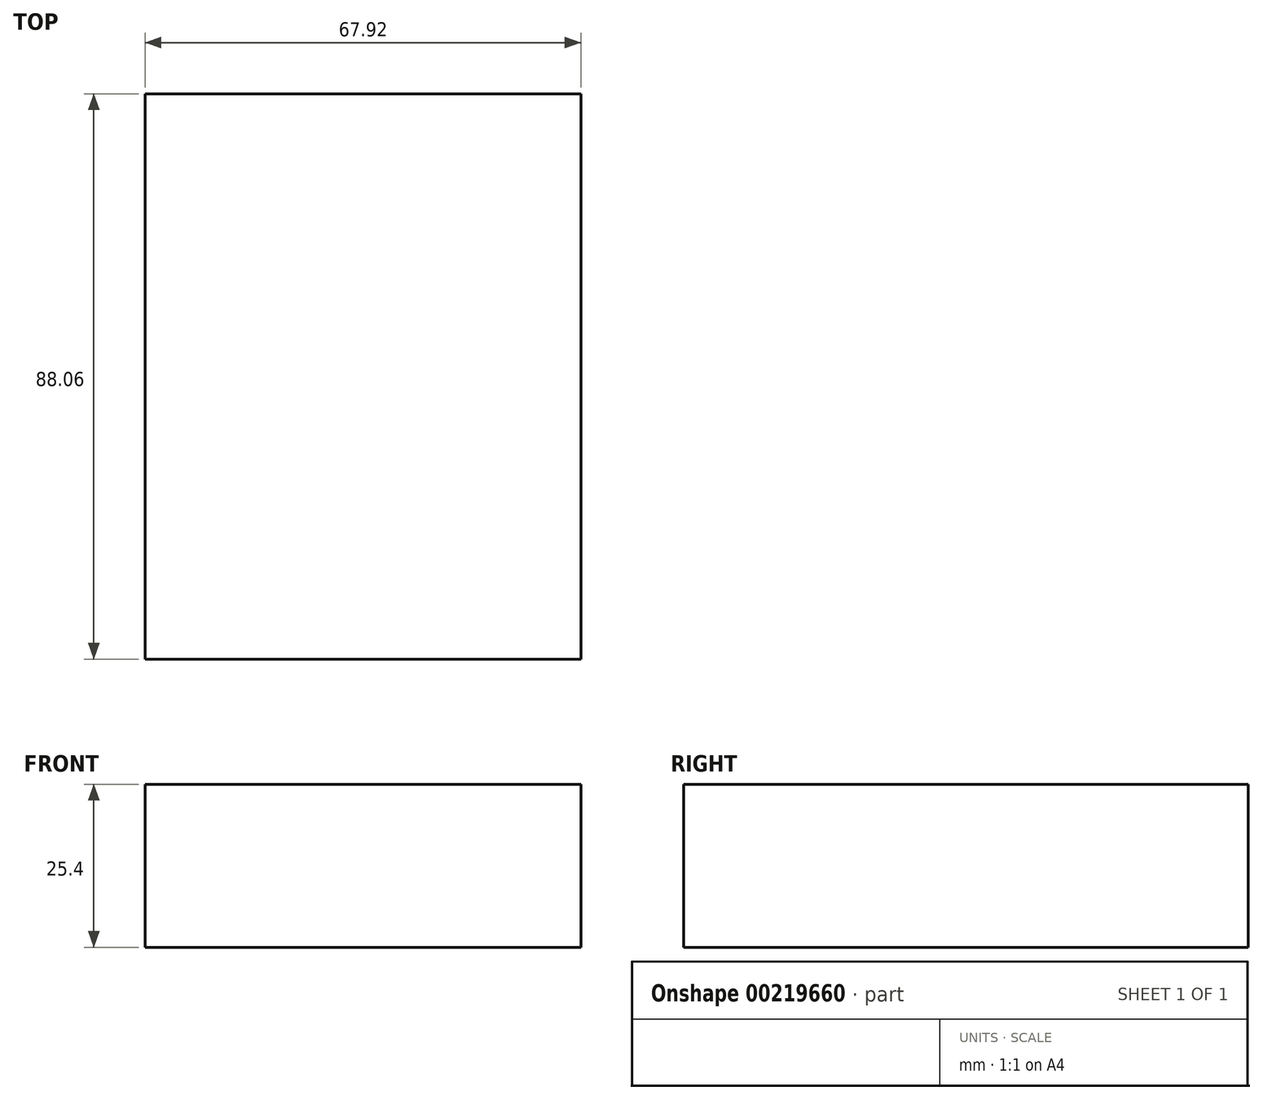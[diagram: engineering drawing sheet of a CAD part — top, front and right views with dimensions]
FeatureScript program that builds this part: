
annotation { "Feature Type Name" : "Feature", "Feature Type Description" : "" }
export const myFeature = defineFeature(function(context is Context, id is Id, definition is map)
    precondition{}
    {
        {
            var Q0;
            Q0=qCreatedBy(makeId("Top.planeOp"),FACE);
            var sketch = newSketch(context, id + "F0", { "sketchPlane" : qUnion([Q0])});
            skLineSegment(sketch, "E0.bottom", {"start": v(33.96, 44.03) * mm, "end": v(-33.96, 44.03) * mm});
            skLineSegment(sketch, "E0.top", {"start": v(33.96, -44.03) * mm, "end": v(-33.96, -44.03) * mm});
            skLineSegment(sketch, "E0.left", {"start": v(33.96, 44.03) * mm, "end": v(33.96, -44.03) * mm});
            skLineSegment(sketch, "E0.right", {"start": v(-33.96, 44.03) * mm, "end": v(-33.96, -44.03) * mm});
            skPoint(sketch, "E0.middle", {"position": v(0, 0) * mm});
            skSolve(sketch);
        }
        {
            var Q0;
            Q0=makeQuery(id+"F0.imprint","IMPRINT",FACE,{"disambiguationData":[TD([[makeQuery(id+"F0.imprint","IMPRINT",EDGE,{"derivedFrom":sQuery(id+"F0.wireOp",EDGE,"E0.bottom")}),1.0]])]});
            extrude(context, id + "F1", {"entities" : qUnion([Q0]), "depth" : 25.4 * mm});
        }
    });
